# Revit family: P710100-031
name_source: partatom
category: Lighting Fixtures
units: mm (PartAtom-declared; Revit-internal decimal feet)

## family parameters
Cut with Voids When Loaded = No
Host = Face
Light Source = Yes
OmniClass Number = 23.80.70.11.14.11
OmniClass Title = Downlights
Part Type = Normal
Room Calculation Point = No
Round Connector Dimension = Use Diameter
Shared = No

## types (1)
- P710100-031
    Apparent Load = 60 VA
    Certifications = • cCSAus certified to UL 1598
• Wall Mount: Suitable for wet locations
• Surface & Pendant Mount: Suitable for wet
locations under covered ceiling
• Cord Mount and all Wall Wash: Suitable for
damp locations
    Color Filter = 16777215
    Default Elevation = 48 "
    Description = Lowery Collection One-Light Textured Black/Distressed Gold Wall Sconce Light
    Dimming Lamp Color Temperature Shift = <None>
    Features = Raise the bar on contemporary design with the Lowery Collection 1-Light Black/Distressed Gold Modern Hanging Pendant Light. Layered rectangular shields coated in a textured black iron finish are artistically combined with distressed gold leaf panels against a black frame. Light sources glowing from inside the structure cast a shimmering reflective light that highlights the beautiful contrast between light and dark.
Application: Raise the bar on contemporary design with the Lowery Collection 1-Light Black/Distressed Gold Modern Hanging Pendant Light is ideal for any entryway, hallway, foyer, bedroom, sitting room, living room, or bathroom.
Styles: Perfect for contemporary and modern style settings.
Finish: Layered rectangular shields coated in a textured black iron finish are artistically combined with distressed gold leaf panels against a black frame.
Materials: Constructed from steel to ensure a long product lifespan.
Glass/Shades: Light sources glowing from inside the structure cast a shimmering reflective light that highlights the beautiful contrast between light and dark.
Bulbs: For ideal illumination, use 1 candelabra base bulb that is sold separately (60w max - LED/CFL/incandescent). Compatible with dimmable bulbs.
Dimensions: Measures 5-3/8-inch width by 15-1/8-inch height.
Certifications: cULus damp location listed.
Pairs With: Pairs with the Adagio, Orrizo, and Rae collections from Progress Lighting.
Warranty: Our 1-Year Limited Warranty guarantees your complete satisfaction with your purchase and includes professional after-sales customer service support.
    Glass = Glass - Hubbell - White
    Gold = Paint - Hubbell - Gold
    Housing Material = Paint - Hubbell -Black
    Lamp = LED/CFL/incandescent
    Manufacturer = Progress Lighting
    Model = P710100-031
    Photometric Web File = Generic.ies
    Product Documentation Link = https://hubbellcdn.com
    Product Page URL = https://www.hubbell.com
    Tilt Angle = 180.00°
    URL = https://www.hubbell.com
    Voltage = 120 V
    Warranty = 1 year warranty
    Wattage Comments = 60W

## geometry (parser evidence)
native form markers: Sweep x1
no freeform markers — native parametric forms only
